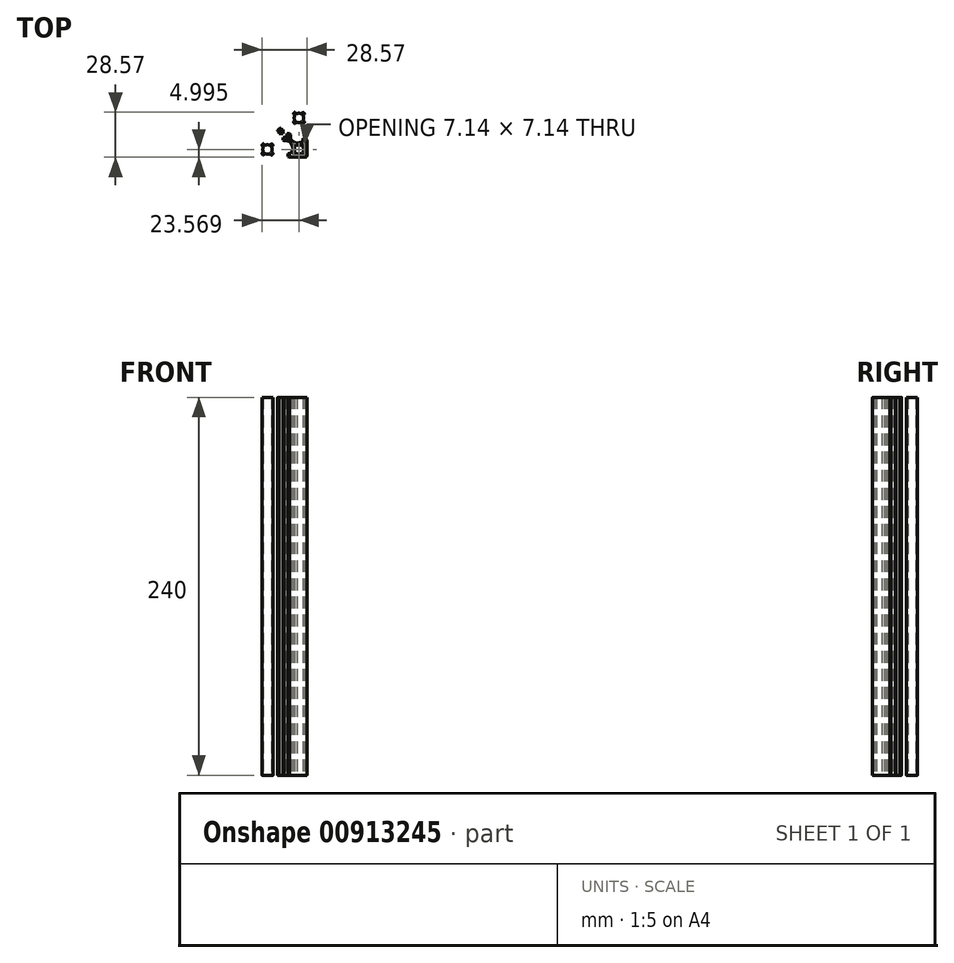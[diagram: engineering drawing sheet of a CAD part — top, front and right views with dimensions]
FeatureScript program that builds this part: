
annotation { "Feature Type Name" : "Feature", "Feature Type Description" : "" }
export const myFeature = defineFeature(function(context is Context, id is Id, definition is map)
    precondition{}
    {
        {
            var Q0;
            Q0=qCreatedBy(makeId("Top.planeOp"),FACE);
            var sketch = newSketch(context, id + "F0", { "sketchPlane" : qUnion([Q0])});
            skLineSegment(sketch, "E0", {"start": v(-2.82, -20.25) * mm, "end": v(-2.82, -15.85) * mm});
            skLineSegment(sketch, "E1", {"start": v(-5.02, -18.05) * mm, "end": v(-0.62, -18.05) * mm});
            skArc(sketch, "E2", {"start": v(-5.5, -19.39) * mm, "mid": v(-5.48, -19.57) * mm, "end": v(-5.56, -19.74) * mm});
            skLineSegment(sketch, "E3", {"start": v(-5.56, -19.74) * mm, "end": v(-6.3, -20.48) * mm});
            skArc(sketch, "E4", {"start": v(-6.3, -20.48) * mm, "mid": v(-6.4, -20.67) * mm, "end": v(-6.32, -20.88) * mm});
            skArc(sketch, "E5", {"start": v(-6.32, -20.88) * mm, "mid": v(-6, -21.24) * mm, "end": v(-5.64, -21.56) * mm});
            skArc(sketch, "E6", {"start": v(-5.64, -21.56) * mm, "mid": v(-5.44, -21.62) * mm, "end": v(-5.24, -21.54) * mm});
            skLineSegment(sketch, "E7", {"start": v(-5.24, -21.54) * mm, "end": v(-4.5, -20.8) * mm});
            skArc(sketch, "E8", {"start": v(-4.5, -20.8) * mm, "mid": v(-4.34, -20.71) * mm, "end": v(-4.16, -20.74) * mm});
            skArc(sketch, "E9", {"start": v(-4.16, -20.74) * mm, "mid": v(-2.82, -21.05) * mm, "end": v(-1.48, -20.74) * mm});
            skArc(sketch, "E10", {"start": v(-1.48, -20.74) * mm, "mid": v(-1.3, -20.71) * mm, "end": v(-1.14, -20.8) * mm});
            skLineSegment(sketch, "E11", {"start": v(-1.14, -20.8) * mm, "end": v(-0.4, -21.54) * mm});
            skArc(sketch, "E12", {"start": v(-0.4, -21.54) * mm, "mid": v(-0.2, -21.62) * mm, "end": v(0, -21.56) * mm});
            skArc(sketch, "E13", {"start": v(0, -21.56) * mm, "mid": v(0.36, -21.24) * mm, "end": v(0.68, -20.88) * mm});
            skArc(sketch, "E14", {"start": v(0.68, -20.88) * mm, "mid": v(0.75, -20.67) * mm, "end": v(0.66, -20.48) * mm});
            skLineSegment(sketch, "E15", {"start": v(0.66, -20.48) * mm, "end": v(-0.08, -19.74) * mm});
            skArc(sketch, "E16", {"start": v(-0.08, -19.74) * mm, "mid": v(-0.16, -19.57) * mm, "end": v(-0.13, -19.39) * mm});
            skArc(sketch, "E17", {"start": v(-0.13, -19.39) * mm, "mid": v(0.18, -18.05) * mm, "end": v(-0.13, -16.72) * mm});
            skArc(sketch, "E18", {"start": v(-0.13, -16.72) * mm, "mid": v(-0.16, -16.54) * mm, "end": v(-0.08, -16.37) * mm});
            skLineSegment(sketch, "E19", {"start": v(-0.08, -16.37) * mm, "end": v(0.66, -15.63) * mm});
            skArc(sketch, "E20", {"start": v(0.66, -15.63) * mm, "mid": v(0.75, -15.44) * mm, "end": v(0.68, -15.23) * mm});
            skArc(sketch, "E21", {"start": v(0.68, -15.23) * mm, "mid": v(0.36, -14.87) * mm, "end": v(0, -14.55) * mm});
            skArc(sketch, "E22", {"start": v(0, -14.55) * mm, "mid": v(-0.2, -14.48) * mm, "end": v(-0.4, -14.57) * mm});
            skLineSegment(sketch, "E23", {"start": v(-0.4, -14.57) * mm, "end": v(-1.14, -15.31) * mm});
            skArc(sketch, "E24", {"start": v(-1.14, -15.31) * mm, "mid": v(-1.3, -15.4) * mm, "end": v(-1.48, -15.37) * mm});
            skArc(sketch, "E25", {"start": v(-1.48, -15.37) * mm, "mid": v(-2.82, -15.05) * mm, "end": v(-4.16, -15.37) * mm});
            skArc(sketch, "E26", {"start": v(-4.16, -15.37) * mm, "mid": v(-4.34, -15.4) * mm, "end": v(-4.5, -15.31) * mm});
            skLineSegment(sketch, "E27", {"start": v(-4.5, -15.31) * mm, "end": v(-5.24, -14.57) * mm});
            skArc(sketch, "E28", {"start": v(-5.24, -14.57) * mm, "mid": v(-5.44, -14.48) * mm, "end": v(-5.64, -14.55) * mm});
            skArc(sketch, "E29", {"start": v(-5.64, -14.55) * mm, "mid": v(-6, -14.87) * mm, "end": v(-6.32, -15.23) * mm});
            skArc(sketch, "E30", {"start": v(-6.32, -15.23) * mm, "mid": v(-6.4, -15.44) * mm, "end": v(-6.3, -15.63) * mm});
            skLineSegment(sketch, "E31", {"start": v(-6.3, -15.63) * mm, "end": v(-5.56, -16.37) * mm});
            skArc(sketch, "E32", {"start": v(-5.56, -16.37) * mm, "mid": v(-5.48, -16.54) * mm, "end": v(-5.5, -16.72) * mm});
            skArc(sketch, "E33", {"start": v(-5.5, -16.72) * mm, "mid": v(-5.82, -18.05) * mm, "end": v(-5.5, -19.39) * mm});
            skLineSegment(sketch, "E34", {"start": v(-5.02, -38.05) * mm, "end": v(-0.62, -38.05) * mm});
            skLineSegment(sketch, "E35", {"start": v(-2.82, -35.85) * mm, "end": v(-2.82, -40.25) * mm});
            skArc(sketch, "E36", {"start": v(-5.5, -36.72) * mm, "mid": v(-5.48, -36.54) * mm, "end": v(-5.56, -36.37) * mm});
            skLineSegment(sketch, "E37", {"start": v(-5.56, -36.37) * mm, "end": v(-6.3, -35.63) * mm});
            skArc(sketch, "E38", {"start": v(-6.3, -35.63) * mm, "mid": v(-6.4, -35.44) * mm, "end": v(-6.33, -35.23) * mm});
            skArc(sketch, "E39", {"start": v(-6.33, -35.23) * mm, "mid": v(-6, -34.87) * mm, "end": v(-5.64, -34.55) * mm});
            skArc(sketch, "E40", {"start": v(-5.64, -34.55) * mm, "mid": v(-5.44, -34.48) * mm, "end": v(-5.24, -34.57) * mm});
            skLineSegment(sketch, "E41", {"start": v(-5.24, -34.57) * mm, "end": v(-4.5, -35.31) * mm});
            skArc(sketch, "E42", {"start": v(-4.5, -35.31) * mm, "mid": v(-4.34, -35.4) * mm, "end": v(-4.16, -35.37) * mm});
            skArc(sketch, "E43", {"start": v(-4.16, -35.37) * mm, "mid": v(-2.82, -35.05) * mm, "end": v(-1.48, -35.37) * mm});
            skArc(sketch, "E44", {"start": v(-1.48, -35.37) * mm, "mid": v(-1.3, -35.4) * mm, "end": v(-1.14, -35.31) * mm});
            skLineSegment(sketch, "E45", {"start": v(-1.14, -35.31) * mm, "end": v(-0.4, -34.57) * mm});
            skArc(sketch, "E46", {"start": v(-0.4, -34.57) * mm, "mid": v(-0.2, -34.48) * mm, "end": v(0, -34.55) * mm});
            skArc(sketch, "E47", {"start": v(0, -34.55) * mm, "mid": v(0.36, -34.87) * mm, "end": v(0.68, -35.23) * mm});
            skArc(sketch, "E48", {"start": v(0.68, -35.23) * mm, "mid": v(0.75, -35.44) * mm, "end": v(0.66, -35.63) * mm});
            skLineSegment(sketch, "E49", {"start": v(0.66, -35.63) * mm, "end": v(-0.08, -36.37) * mm});
            skArc(sketch, "E50", {"start": v(-0.08, -36.37) * mm, "mid": v(-0.16, -36.54) * mm, "end": v(-0.13, -36.72) * mm});
            skArc(sketch, "E51", {"start": v(-0.13, -36.72) * mm, "mid": v(0.18, -38.05) * mm, "end": v(-0.14, -39.4) * mm});
            skArc(sketch, "E52", {"start": v(-0.14, -39.4) * mm, "mid": v(-0.16, -39.57) * mm, "end": v(-0.08, -39.74) * mm});
            skLineSegment(sketch, "E53", {"start": v(-0.08, -39.74) * mm, "end": v(0.66, -40.48) * mm});
            skArc(sketch, "E54", {"start": v(0.66, -40.48) * mm, "mid": v(0.75, -40.67) * mm, "end": v(0.68, -40.88) * mm});
            skArc(sketch, "E55", {"start": v(0.68, -40.88) * mm, "mid": v(0.36, -41.24) * mm, "end": v(0, -41.56) * mm});
            skArc(sketch, "E56", {"start": v(0, -41.56) * mm, "mid": v(-0.2, -41.63) * mm, "end": v(-0.4, -41.54) * mm});
            skLineSegment(sketch, "E57", {"start": v(-0.4, -41.54) * mm, "end": v(-1.14, -40.8) * mm});
            skArc(sketch, "E58", {"start": v(-1.14, -40.8) * mm, "mid": v(-1.3, -40.71) * mm, "end": v(-1.49, -40.74) * mm});
            skArc(sketch, "E59", {"start": v(-1.49, -40.74) * mm, "mid": v(-2.82, -41.05) * mm, "end": v(-4.16, -40.74) * mm});
            skArc(sketch, "E60", {"start": v(-4.16, -40.74) * mm, "mid": v(-4.34, -40.71) * mm, "end": v(-4.5, -40.8) * mm});
            skLineSegment(sketch, "E61", {"start": v(-4.5, -40.8) * mm, "end": v(-5.24, -41.54) * mm});
            skArc(sketch, "E62", {"start": v(-5.24, -41.54) * mm, "mid": v(-5.44, -41.62) * mm, "end": v(-5.64, -41.56) * mm});
            skArc(sketch, "E63", {"start": v(-5.64, -41.56) * mm, "mid": v(-6, -41.24) * mm, "end": v(-6.33, -40.88) * mm});
            skArc(sketch, "E64", {"start": v(-6.33, -40.88) * mm, "mid": v(-6.4, -40.67) * mm, "end": v(-6.3, -40.48) * mm});
            skLineSegment(sketch, "E65", {"start": v(-6.3, -40.48) * mm, "end": v(-5.56, -39.74) * mm});
            skArc(sketch, "E66", {"start": v(-5.56, -39.74) * mm, "mid": v(-5.48, -39.57) * mm, "end": v(-5.5, -39.4) * mm});
            skArc(sketch, "E67", {"start": v(-5.5, -39.4) * mm, "mid": v(-5.82, -38.05) * mm, "end": v(-5.5, -36.72) * mm});
            skArc(sketch, "E68", {"start": v(-20.13, -36.72) * mm, "mid": v(-20.16, -36.54) * mm, "end": v(-20.07, -36.37) * mm});
            skLineSegment(sketch, "E69", {"start": v(-20.07, -36.37) * mm, "end": v(-19.33, -35.63) * mm});
            skArc(sketch, "E70", {"start": v(-19.33, -35.63) * mm, "mid": v(-19.25, -35.44) * mm, "end": v(-19.31, -35.23) * mm});
            skArc(sketch, "E71", {"start": v(-19.31, -35.23) * mm, "mid": v(-19.64, -34.87) * mm, "end": v(-20, -34.55) * mm});
            skArc(sketch, "E72", {"start": v(-20, -34.55) * mm, "mid": v(-20.2, -34.48) * mm, "end": v(-20.4, -34.57) * mm});
            skLineSegment(sketch, "E73", {"start": v(-20.4, -34.57) * mm, "end": v(-21.14, -35.31) * mm});
            skArc(sketch, "E74", {"start": v(-21.14, -35.31) * mm, "mid": v(-21.3, -35.4) * mm, "end": v(-21.48, -35.37) * mm});
            skArc(sketch, "E75", {"start": v(-21.48, -35.37) * mm, "mid": v(-22.82, -35.05) * mm, "end": v(-24.15, -35.37) * mm});
            skArc(sketch, "E76", {"start": v(-24.15, -35.37) * mm, "mid": v(-24.34, -35.4) * mm, "end": v(-24.5, -35.31) * mm});
            skLineSegment(sketch, "E77", {"start": v(-24.5, -35.31) * mm, "end": v(-25.24, -34.57) * mm});
            skArc(sketch, "E78", {"start": v(-25.24, -34.57) * mm, "mid": v(-25.44, -34.48) * mm, "end": v(-25.64, -34.55) * mm});
            skArc(sketch, "E79", {"start": v(-25.64, -34.55) * mm, "mid": v(-26, -34.87) * mm, "end": v(-26.32, -35.23) * mm});
            skArc(sketch, "E80", {"start": v(-26.32, -35.23) * mm, "mid": v(-26.39, -35.44) * mm, "end": v(-26.3, -35.63) * mm});
            skLineSegment(sketch, "E81", {"start": v(-26.3, -35.63) * mm, "end": v(-25.56, -36.37) * mm});
            skArc(sketch, "E82", {"start": v(-25.56, -36.37) * mm, "mid": v(-25.48, -36.54) * mm, "end": v(-25.5, -36.72) * mm});
            skArc(sketch, "E83", {"start": v(-25.5, -36.72) * mm, "mid": v(-25.82, -38.05) * mm, "end": v(-25.5, -39.4) * mm});
            skArc(sketch, "E84", {"start": v(-25.5, -39.4) * mm, "mid": v(-25.48, -39.57) * mm, "end": v(-25.56, -39.74) * mm});
            skLineSegment(sketch, "E85", {"start": v(-25.56, -39.74) * mm, "end": v(-26.3, -40.48) * mm});
            skArc(sketch, "E86", {"start": v(-26.3, -40.48) * mm, "mid": v(-26.39, -40.67) * mm, "end": v(-26.32, -40.88) * mm});
            skArc(sketch, "E87", {"start": v(-26.32, -40.88) * mm, "mid": v(-26, -41.24) * mm, "end": v(-25.64, -41.56) * mm});
            skArc(sketch, "E88", {"start": v(-25.64, -41.56) * mm, "mid": v(-25.44, -41.63) * mm, "end": v(-25.24, -41.54) * mm});
            skLineSegment(sketch, "E89", {"start": v(-25.24, -41.54) * mm, "end": v(-24.5, -40.8) * mm});
            skArc(sketch, "E90", {"start": v(-24.5, -40.8) * mm, "mid": v(-24.33, -40.71) * mm, "end": v(-24.15, -40.74) * mm});
            skArc(sketch, "E91", {"start": v(-24.15, -40.74) * mm, "mid": v(-22.82, -41.05) * mm, "end": v(-21.48, -40.74) * mm});
            skArc(sketch, "E92", {"start": v(-21.48, -40.74) * mm, "mid": v(-21.3, -40.71) * mm, "end": v(-21.14, -40.8) * mm});
            skLineSegment(sketch, "E93", {"start": v(-21.14, -40.8) * mm, "end": v(-20.4, -41.54) * mm});
            skArc(sketch, "E94", {"start": v(-20.4, -41.54) * mm, "mid": v(-20.2, -41.62) * mm, "end": v(-20, -41.56) * mm});
            skArc(sketch, "E95", {"start": v(-20, -41.56) * mm, "mid": v(-19.63, -41.24) * mm, "end": v(-19.31, -40.88) * mm});
            skArc(sketch, "E96", {"start": v(-19.31, -40.88) * mm, "mid": v(-19.25, -40.67) * mm, "end": v(-19.33, -40.48) * mm});
            skLineSegment(sketch, "E97", {"start": v(-19.33, -40.48) * mm, "end": v(-20.07, -39.74) * mm});
            skArc(sketch, "E98", {"start": v(-20.07, -39.74) * mm, "mid": v(-20.16, -39.57) * mm, "end": v(-20.13, -39.4) * mm});
            skArc(sketch, "E99", {"start": v(-20.13, -39.4) * mm, "mid": v(-19.82, -38.05) * mm, "end": v(-20.13, -36.72) * mm});
            skLineSegment(sketch, "E100", {"start": v(-22.82, -35.85) * mm, "end": v(-22.82, -40.25) * mm});
            skLineSegment(sketch, "E101", {"start": v(-20.62, -38.05) * mm, "end": v(-25.02, -38.05) * mm});
            skLineSegment(sketch, "E102", {"start": v(-20.62, -18.05) * mm, "end": v(-25.02, -18.05) * mm});
            skLineSegment(sketch, "E103", {"start": v(-22.82, -20.25) * mm, "end": v(-22.82, -15.85) * mm});
            skLineSegment(sketch, "E104", {"start": v(2.64, -28.05) * mm, "end": v(-29.04, -28.05) * mm});
            skLineSegment(sketch, "E105", {"start": v(-12.82, -44) * mm, "end": v(-12.82, -12.06) * mm});
            skArc(sketch, "E106", {"start": v(-9.58, -26.47) * mm, "mid": v(-9.36, -26.3) * mm, "end": v(-9.38, -26.02) * mm});
            skArc(sketch, "E107", {"start": v(-9.38, -26.02) * mm, "mid": v(-10, -25.23) * mm, "end": v(-10.78, -24.61) * mm});
            skArc(sketch, "E108", {"start": v(-10.78, -24.61) * mm, "mid": v(-11.06, -24.6) * mm, "end": v(-11.23, -24.82) * mm});
            skLineSegment(sketch, "E109", {"start": v(-11.23, -24.82) * mm, "end": v(-11.37, -25.56) * mm});
            skArc(sketch, "E110", {"start": v(-11.37, -25.56) * mm, "mid": v(-11.52, -25.77) * mm, "end": v(-11.78, -25.78) * mm});
            skArc(sketch, "E111", {"start": v(-11.78, -25.78) * mm, "mid": v(-12.82, -25.55) * mm, "end": v(-13.85, -25.78) * mm});
            skArc(sketch, "E112", {"start": v(-13.85, -25.78) * mm, "mid": v(-14.11, -25.77) * mm, "end": v(-14.27, -25.56) * mm});
            skLineSegment(sketch, "E113", {"start": v(-14.27, -25.56) * mm, "end": v(-14.4, -24.82) * mm});
            skArc(sketch, "E114", {"start": v(-14.4, -24.82) * mm, "mid": v(-14.57, -24.6) * mm, "end": v(-14.85, -24.61) * mm});
            skArc(sketch, "E115", {"start": v(-14.85, -24.61) * mm, "mid": v(-15.65, -25.23) * mm, "end": v(-16.26, -26.02) * mm});
            skArc(sketch, "E116", {"start": v(-16.26, -26.02) * mm, "mid": v(-16.27, -26.3) * mm, "end": v(-16.06, -26.47) * mm});
            skLineSegment(sketch, "E117", {"start": v(-16.06, -26.47) * mm, "end": v(-15.31, -26.6) * mm});
            skArc(sketch, "E118", {"start": v(-15.31, -26.6) * mm, "mid": v(-15.1, -26.76) * mm, "end": v(-15.1, -27.02) * mm});
            skArc(sketch, "E119", {"start": v(-15.1, -27.02) * mm, "mid": v(-15.32, -28.05) * mm, "end": v(-15.1, -29.09) * mm});
            skArc(sketch, "E120", {"start": v(-15.1, -29.09) * mm, "mid": v(-15.1, -29.35) * mm, "end": v(-15.31, -29.5) * mm});
            skLineSegment(sketch, "E121", {"start": v(-15.31, -29.5) * mm, "end": v(-16.06, -29.64) * mm});
            skArc(sketch, "E122", {"start": v(-16.06, -29.64) * mm, "mid": v(-16.27, -29.81) * mm, "end": v(-16.26, -30.09) * mm});
            skArc(sketch, "E123", {"start": v(-16.26, -30.09) * mm, "mid": v(-15.65, -30.88) * mm, "end": v(-14.85, -31.5) * mm});
            skArc(sketch, "E124", {"start": v(-14.85, -31.5) * mm, "mid": v(-14.57, -31.51) * mm, "end": v(-14.4, -31.3) * mm});
            skLineSegment(sketch, "E125", {"start": v(-14.4, -31.3) * mm, "end": v(-14.27, -30.55) * mm});
            skArc(sketch, "E126", {"start": v(-14.27, -30.55) * mm, "mid": v(-14.11, -30.34) * mm, "end": v(-13.85, -30.33) * mm});
            skArc(sketch, "E127", {"start": v(-13.85, -30.33) * mm, "mid": v(-12.82, -30.55) * mm, "end": v(-11.78, -30.33) * mm});
            skArc(sketch, "E128", {"start": v(-11.78, -30.33) * mm, "mid": v(-11.52, -30.34) * mm, "end": v(-11.37, -30.55) * mm});
            skLineSegment(sketch, "E129", {"start": v(-11.37, -30.55) * mm, "end": v(-11.23, -31.3) * mm});
            skArc(sketch, "E130", {"start": v(-11.23, -31.3) * mm, "mid": v(-11.06, -31.51) * mm, "end": v(-10.78, -31.5) * mm});
            skArc(sketch, "E131", {"start": v(-10.78, -31.5) * mm, "mid": v(-10, -30.88) * mm, "end": v(-9.38, -30.09) * mm});
            skArc(sketch, "E132", {"start": v(-9.38, -30.09) * mm, "mid": v(-9.36, -29.81) * mm, "end": v(-9.58, -29.64) * mm});
            skLineSegment(sketch, "E133", {"start": v(-9.58, -29.64) * mm, "end": v(-10.32, -29.5) * mm});
            skArc(sketch, "E134", {"start": v(-10.32, -29.5) * mm, "mid": v(-10.53, -29.35) * mm, "end": v(-10.54, -29.09) * mm});
            skArc(sketch, "E135", {"start": v(-10.54, -29.09) * mm, "mid": v(-10.32, -28.05) * mm, "end": v(-10.54, -27.02) * mm});
            skArc(sketch, "E136", {"start": v(-10.54, -27.02) * mm, "mid": v(-10.53, -26.76) * mm, "end": v(-10.32, -26.6) * mm});
            skLineSegment(sketch, "E137", {"start": v(-10.32, -26.6) * mm, "end": v(-9.58, -26.47) * mm});
            skArc(sketch, "E138", {"start": v(-20.13, -19.39) * mm, "mid": v(-20.16, -19.57) * mm, "end": v(-20.08, -19.74) * mm});
            skLineSegment(sketch, "E139", {"start": v(-20.08, -19.74) * mm, "end": v(-19.33, -20.48) * mm});
            skArc(sketch, "E140", {"start": v(-19.33, -20.48) * mm, "mid": v(-19.25, -20.67) * mm, "end": v(-19.31, -20.88) * mm});
            skArc(sketch, "E141", {"start": v(-19.31, -20.88) * mm, "mid": v(-19.64, -21.24) * mm, "end": v(-20, -21.56) * mm});
            skArc(sketch, "E142", {"start": v(-20, -21.56) * mm, "mid": v(-20.2, -21.62) * mm, "end": v(-20.4, -21.54) * mm});
            skLineSegment(sketch, "E143", {"start": v(-20.4, -21.54) * mm, "end": v(-21.14, -20.8) * mm});
            skArc(sketch, "E144", {"start": v(-21.14, -20.8) * mm, "mid": v(-21.3, -20.71) * mm, "end": v(-21.48, -20.74) * mm});
            skArc(sketch, "E145", {"start": v(-21.48, -20.74) * mm, "mid": v(-22.82, -21.05) * mm, "end": v(-24.15, -20.74) * mm});
            skArc(sketch, "E146", {"start": v(-24.15, -20.74) * mm, "mid": v(-24.34, -20.71) * mm, "end": v(-24.5, -20.8) * mm});
            skLineSegment(sketch, "E147", {"start": v(-24.5, -20.8) * mm, "end": v(-25.24, -21.54) * mm});
            skArc(sketch, "E148", {"start": v(-25.24, -21.54) * mm, "mid": v(-25.44, -21.62) * mm, "end": v(-25.64, -21.56) * mm});
            skArc(sketch, "E149", {"start": v(-25.64, -21.56) * mm, "mid": v(-26, -21.24) * mm, "end": v(-26.32, -20.88) * mm});
            skArc(sketch, "E150", {"start": v(-26.32, -20.88) * mm, "mid": v(-26.39, -20.67) * mm, "end": v(-26.3, -20.48) * mm});
            skLineSegment(sketch, "E151", {"start": v(-26.3, -20.48) * mm, "end": v(-25.56, -19.74) * mm});
            skArc(sketch, "E152", {"start": v(-25.56, -19.74) * mm, "mid": v(-25.48, -19.57) * mm, "end": v(-25.5, -19.39) * mm});
            skArc(sketch, "E153", {"start": v(-25.5, -19.39) * mm, "mid": v(-25.82, -18.05) * mm, "end": v(-25.5, -16.72) * mm});
            skArc(sketch, "E154", {"start": v(-25.5, -16.72) * mm, "mid": v(-25.48, -16.54) * mm, "end": v(-25.56, -16.37) * mm});
            skLineSegment(sketch, "E155", {"start": v(-25.56, -16.37) * mm, "end": v(-26.3, -15.63) * mm});
            skArc(sketch, "E156", {"start": v(-26.3, -15.63) * mm, "mid": v(-26.39, -15.44) * mm, "end": v(-26.32, -15.23) * mm});
            skArc(sketch, "E157", {"start": v(-26.32, -15.23) * mm, "mid": v(-26, -14.87) * mm, "end": v(-25.64, -14.55) * mm});
            skArc(sketch, "E158", {"start": v(-25.64, -14.55) * mm, "mid": v(-25.44, -14.48) * mm, "end": v(-25.24, -14.57) * mm});
            skLineSegment(sketch, "E159", {"start": v(-25.24, -14.57) * mm, "end": v(-24.5, -15.31) * mm});
            skArc(sketch, "E160", {"start": v(-24.5, -15.31) * mm, "mid": v(-24.34, -15.4) * mm, "end": v(-24.15, -15.37) * mm});
            skArc(sketch, "E161", {"start": v(-24.15, -15.37) * mm, "mid": v(-22.82, -15.05) * mm, "end": v(-21.48, -15.37) * mm});
            skArc(sketch, "E162", {"start": v(-21.48, -15.37) * mm, "mid": v(-21.3, -15.4) * mm, "end": v(-21.14, -15.31) * mm});
            skLineSegment(sketch, "E163", {"start": v(-21.14, -15.31) * mm, "end": v(-20.4, -14.57) * mm});
            skArc(sketch, "E164", {"start": v(-20.4, -14.57) * mm, "mid": v(-20.2, -14.48) * mm, "end": v(-20, -14.55) * mm});
            skArc(sketch, "E165", {"start": v(-20, -14.55) * mm, "mid": v(-19.64, -14.87) * mm, "end": v(-19.31, -15.23) * mm});
            skArc(sketch, "E166", {"start": v(-19.31, -15.23) * mm, "mid": v(-19.25, -15.44) * mm, "end": v(-19.33, -15.63) * mm});
            skLineSegment(sketch, "E167", {"start": v(-19.33, -15.63) * mm, "end": v(-20.08, -16.37) * mm});
            skArc(sketch, "E168", {"start": v(-20.08, -16.37) * mm, "mid": v(-20.16, -16.54) * mm, "end": v(-20.13, -16.72) * mm});
            skArc(sketch, "E169", {"start": v(-20.13, -16.72) * mm, "mid": v(-19.82, -18.05) * mm, "end": v(-20.13, -19.39) * mm});
            skLineSegment(sketch, "E170", {"start": v(-8.87, -43.05) * mm, "end": v(-9.67, -42.55) * mm});
            skLineSegment(sketch, "E171", {"start": v(-9.67, -42.55) * mm, "end": v(-9.67, -40.85) * mm});
            skArc(sketch, "E172", {"start": v(-9.67, -40.85) * mm, "mid": v(-9.58, -40.64) * mm, "end": v(-9.37, -40.55) * mm});
            skLineSegment(sketch, "E173", {"start": v(-9.37, -40.55) * mm, "end": v(-7.72, -40.55) * mm});
            skLineSegment(sketch, "E174", {"start": v(-7.72, -40.55) * mm, "end": v(-6.73, -37.5) * mm});
            skArc(sketch, "E175", {"start": v(-6.73, -37.5) * mm, "mid": v(-6.68, -37.24) * mm, "end": v(-6.7, -36.98) * mm});
            skArc(sketch, "E176", {"start": v(-6.7, -36.98) * mm, "mid": v(-7.54, -34.94) * mm, "end": v(-8.81, -33.14) * mm});
            skArc(sketch, "E177", {"start": v(-8.81, -33.14) * mm, "mid": v(-9.66, -32.7) * mm, "end": v(-10.6, -32.55) * mm});
            skLineSegment(sketch, "E178", {"start": v(-10.6, -32.55) * mm, "end": v(-12.32, -32.55) * mm});
            skLineSegment(sketch, "E179", {"start": v(-12.32, -32.55) * mm, "end": v(-12.82, -32.05) * mm});
            skLineSegment(sketch, "E180", {"start": v(-12.82, -32.05) * mm, "end": v(-13.32, -32.55) * mm});
            skLineSegment(sketch, "E181", {"start": v(-13.32, -32.55) * mm, "end": v(-15.04, -32.55) * mm});
            skArc(sketch, "E182", {"start": v(-15.04, -32.55) * mm, "mid": v(-15.98, -32.7) * mm, "end": v(-16.82, -33.14) * mm});
            skArc(sketch, "E183", {"start": v(-16.82, -33.14) * mm, "mid": v(-18.1, -34.94) * mm, "end": v(-18.93, -36.98) * mm});
            skArc(sketch, "E184", {"start": v(-18.93, -36.98) * mm, "mid": v(-18.95, -37.24) * mm, "end": v(-18.9, -37.5) * mm});
            skLineSegment(sketch, "E185", {"start": v(-18.9, -37.5) * mm, "end": v(-17.92, -40.55) * mm});
            skLineSegment(sketch, "E186", {"start": v(-17.92, -40.55) * mm, "end": v(-16.27, -40.55) * mm});
            skArc(sketch, "E187", {"start": v(-16.27, -40.55) * mm, "mid": v(-16.06, -40.64) * mm, "end": v(-15.97, -40.85) * mm});
            skLineSegment(sketch, "E188", {"start": v(-15.97, -40.85) * mm, "end": v(-15.97, -42.55) * mm});
            skLineSegment(sketch, "E189", {"start": v(-15.97, -42.55) * mm, "end": v(-16.77, -43.05) * mm});
            skLineSegment(sketch, "E190", {"start": v(-16.77, -43.05) * mm, "end": v(-26.82, -43.05) * mm});
            skArc(sketch, "E191", {"start": v(-26.82, -43.05) * mm, "mid": v(-27.52, -42.76) * mm, "end": v(-27.82, -42.05) * mm});
            skLineSegment(sketch, "E192", {"start": v(-27.82, -42.05) * mm, "end": v(-27.82, -32) * mm});
            skLineSegment(sketch, "E193", {"start": v(-27.82, -32) * mm, "end": v(-27.32, -31.2) * mm});
            skLineSegment(sketch, "E194", {"start": v(-27.32, -31.2) * mm, "end": v(-25.62, -31.2) * mm});
            skArc(sketch, "E195", {"start": v(-25.62, -31.2) * mm, "mid": v(-25.4, -31.3) * mm, "end": v(-25.32, -31.5) * mm});
            skLineSegment(sketch, "E196", {"start": v(-25.32, -31.5) * mm, "end": v(-25.32, -33.15) * mm});
            skLineSegment(sketch, "E197", {"start": v(-25.32, -33.15) * mm, "end": v(-22.27, -34.14) * mm});
            skArc(sketch, "E198", {"start": v(-22.27, -34.14) * mm, "mid": v(-22, -34.19) * mm, "end": v(-21.75, -34.17) * mm});
            skArc(sketch, "E199", {"start": v(-21.75, -34.17) * mm, "mid": v(-19.7, -33.33) * mm, "end": v(-17.9, -32.06) * mm});
            skArc(sketch, "E200", {"start": v(-17.9, -32.06) * mm, "mid": v(-17.47, -31.21) * mm, "end": v(-17.32, -30.27) * mm});
            skLineSegment(sketch, "E201", {"start": v(-17.32, -30.27) * mm, "end": v(-17.32, -28.55) * mm});
            skLineSegment(sketch, "E202", {"start": v(-17.32, -28.55) * mm, "end": v(-16.82, -28.05) * mm});
            skLineSegment(sketch, "E203", {"start": v(-16.82, -28.05) * mm, "end": v(-17.32, -27.55) * mm});
            skLineSegment(sketch, "E204", {"start": v(-17.32, -27.55) * mm, "end": v(-17.32, -25.84) * mm});
            skArc(sketch, "E205", {"start": v(-17.32, -25.84) * mm, "mid": v(-17.47, -24.9) * mm, "end": v(-17.9, -24.05) * mm});
            skArc(sketch, "E206", {"start": v(-17.9, -24.05) * mm, "mid": v(-19.7, -22.78) * mm, "end": v(-21.75, -21.94) * mm});
            skArc(sketch, "E207", {"start": v(-21.75, -21.94) * mm, "mid": v(-22, -21.92) * mm, "end": v(-22.27, -21.97) * mm});
            skLineSegment(sketch, "E208", {"start": v(-22.27, -21.97) * mm, "end": v(-25.32, -22.95) * mm});
            skLineSegment(sketch, "E209", {"start": v(-25.32, -22.95) * mm, "end": v(-25.32, -24.6) * mm});
            skArc(sketch, "E210", {"start": v(-25.32, -24.6) * mm, "mid": v(-25.4, -24.82) * mm, "end": v(-25.62, -24.9) * mm});
            skLineSegment(sketch, "E211", {"start": v(-25.62, -24.9) * mm, "end": v(-27.32, -24.9) * mm});
            skLineSegment(sketch, "E212", {"start": v(-27.32, -24.9) * mm, "end": v(-27.82, -24.1) * mm});
            skLineSegment(sketch, "E213", {"start": v(-27.82, -24.1) * mm, "end": v(-27.82, -14.05) * mm});
            skArc(sketch, "E214", {"start": v(-27.82, -14.05) * mm, "mid": v(-27.52, -13.35) * mm, "end": v(-26.82, -13.05) * mm});
            skLineSegment(sketch, "E215", {"start": v(-26.82, -13.05) * mm, "end": v(-16.77, -13.05) * mm});
            skLineSegment(sketch, "E216", {"start": v(-16.77, -13.05) * mm, "end": v(-15.97, -13.55) * mm});
            skLineSegment(sketch, "E217", {"start": v(-15.97, -13.55) * mm, "end": v(-15.97, -15.25) * mm});
            skArc(sketch, "E218", {"start": v(-15.97, -15.25) * mm, "mid": v(-16.06, -15.47) * mm, "end": v(-16.27, -15.55) * mm});
            skLineSegment(sketch, "E219", {"start": v(-16.27, -15.55) * mm, "end": v(-17.92, -15.55) * mm});
            skLineSegment(sketch, "E220", {"start": v(-17.92, -15.55) * mm, "end": v(-18.9, -18.6) * mm});
            skArc(sketch, "E221", {"start": v(-18.9, -18.6) * mm, "mid": v(-18.95, -18.86) * mm, "end": v(-18.93, -19.13) * mm});
            skArc(sketch, "E222", {"start": v(-18.93, -19.13) * mm, "mid": v(-18.1, -21.16) * mm, "end": v(-16.82, -22.96) * mm});
            skArc(sketch, "E223", {"start": v(-16.82, -22.96) * mm, "mid": v(-15.98, -23.4) * mm, "end": v(-15.04, -23.55) * mm});
            skLineSegment(sketch, "E224", {"start": v(-15.04, -23.55) * mm, "end": v(-13.32, -23.55) * mm});
            skLineSegment(sketch, "E225", {"start": v(-13.32, -23.55) * mm, "end": v(-12.82, -24.05) * mm});
            skLineSegment(sketch, "E226", {"start": v(-12.82, -24.05) * mm, "end": v(-12.32, -23.55) * mm});
            skLineSegment(sketch, "E227", {"start": v(-12.32, -23.55) * mm, "end": v(-10.6, -23.55) * mm});
            skArc(sketch, "E228", {"start": v(-10.6, -23.55) * mm, "mid": v(-9.66, -23.4) * mm, "end": v(-8.81, -22.96) * mm});
            skArc(sketch, "E229", {"start": v(-8.81, -22.96) * mm, "mid": v(-7.54, -21.16) * mm, "end": v(-6.7, -19.13) * mm});
            skArc(sketch, "E230", {"start": v(-6.7, -19.13) * mm, "mid": v(-6.68, -18.86) * mm, "end": v(-6.73, -18.6) * mm});
            skLineSegment(sketch, "E231", {"start": v(-6.73, -18.6) * mm, "end": v(-7.72, -15.55) * mm});
            skLineSegment(sketch, "E232", {"start": v(-7.72, -15.55) * mm, "end": v(-9.37, -15.55) * mm});
            skArc(sketch, "E233", {"start": v(-9.37, -15.55) * mm, "mid": v(-9.58, -15.47) * mm, "end": v(-9.67, -15.25) * mm});
            skLineSegment(sketch, "E234", {"start": v(-9.67, -15.25) * mm, "end": v(-9.67, -13.55) * mm});
            skLineSegment(sketch, "E235", {"start": v(-9.67, -13.55) * mm, "end": v(-8.87, -13.05) * mm});
            skLineSegment(sketch, "E236", {"start": v(-8.87, -13.05) * mm, "end": v(1.18, -13.05) * mm});
            skArc(sketch, "E237", {"start": v(1.18, -13.05) * mm, "mid": v(1.89, -13.35) * mm, "end": v(2.18, -14.05) * mm});
            skLineSegment(sketch, "E238", {"start": v(2.18, -14.05) * mm, "end": v(2.18, -24.1) * mm});
            skLineSegment(sketch, "E239", {"start": v(2.18, -24.1) * mm, "end": v(1.68, -24.9) * mm});
            skLineSegment(sketch, "E240", {"start": v(1.68, -24.9) * mm, "end": v(-0.02, -24.9) * mm});
            skArc(sketch, "E241", {"start": v(-0.02, -24.9) * mm, "mid": v(-0.23, -24.82) * mm, "end": v(-0.32, -24.6) * mm});
            skLineSegment(sketch, "E242", {"start": v(-0.32, -24.6) * mm, "end": v(-0.32, -22.95) * mm});
            skLineSegment(sketch, "E243", {"start": v(-0.32, -22.95) * mm, "end": v(-3.37, -21.97) * mm});
            skArc(sketch, "E244", {"start": v(-3.37, -21.97) * mm, "mid": v(-3.63, -21.92) * mm, "end": v(-3.9, -21.94) * mm});
            skArc(sketch, "E245", {"start": v(-3.9, -21.94) * mm, "mid": v(-5.93, -22.78) * mm, "end": v(-7.73, -24.05) * mm});
            skArc(sketch, "E246", {"start": v(-7.73, -24.05) * mm, "mid": v(-8.17, -24.9) * mm, "end": v(-8.32, -25.84) * mm});
            skLineSegment(sketch, "E247", {"start": v(-8.32, -25.84) * mm, "end": v(-8.32, -27.55) * mm});
            skLineSegment(sketch, "E248", {"start": v(-8.32, -27.55) * mm, "end": v(-8.82, -28.05) * mm});
            skLineSegment(sketch, "E249", {"start": v(-8.82, -28.05) * mm, "end": v(-8.32, -28.55) * mm});
            skLineSegment(sketch, "E250", {"start": v(-8.32, -28.55) * mm, "end": v(-8.32, -30.27) * mm});
            skArc(sketch, "E251", {"start": v(-8.32, -30.27) * mm, "mid": v(-8.17, -31.21) * mm, "end": v(-7.73, -32.06) * mm});
            skArc(sketch, "E252", {"start": v(-7.73, -32.06) * mm, "mid": v(-5.93, -33.33) * mm, "end": v(-3.9, -34.17) * mm});
            skArc(sketch, "E253", {"start": v(-3.9, -34.17) * mm, "mid": v(-3.63, -34.19) * mm, "end": v(-3.37, -34.14) * mm});
            skLineSegment(sketch, "E254", {"start": v(-3.37, -34.14) * mm, "end": v(-0.32, -33.15) * mm});
            skLineSegment(sketch, "E255", {"start": v(-0.32, -33.15) * mm, "end": v(-0.32, -31.5) * mm});
            skArc(sketch, "E256", {"start": v(-0.32, -31.5) * mm, "mid": v(-0.23, -31.3) * mm, "end": v(-0.02, -31.2) * mm});
            skLineSegment(sketch, "E257", {"start": v(-0.02, -31.2) * mm, "end": v(1.68, -31.2) * mm});
            skLineSegment(sketch, "E258", {"start": v(1.68, -31.2) * mm, "end": v(2.18, -32) * mm});
            skLineSegment(sketch, "E259", {"start": v(2.18, -32) * mm, "end": v(2.18, -42.05) * mm});
            skArc(sketch, "E260", {"start": v(2.18, -42.05) * mm, "mid": v(1.89, -42.76) * mm, "end": v(1.18, -43.05) * mm});
            skLineSegment(sketch, "E261", {"start": v(1.18, -43.05) * mm, "end": v(-8.87, -43.05) * mm});
            skSolve(sketch);
        }
        {
            var Q0;
            {var subQ1=sQuery(id+"F0.wireOp",EDGE,"E112");Q0=makeQuery(id+"F0.imprint","IMPRINT",FACE,{"disambiguationData":[TD([[makeQuery(id+"F0.imprint","IMPRINT",EDGE,{"derivedFrom":subQ1}),-1.0]])]});}
            var Q1;
            Q1=makeQuery(id+"F0.imprint","IMPRINT",FACE,{"disambiguationData":[TD([[makeQuery(id+"F0.imprint","IMPRINT",EDGE,{"derivedFrom":sQuery(id+"F0.wireOp",EDGE,"E2")}),-1.0]])]});
            var Q2;
            Q2=makeQuery(id+"F0.imprint","IMPRINT",FACE,{"disambiguationData":[TD([[makeQuery(id+"F0.imprint","IMPRINT",EDGE,{"derivedFrom":sQuery(id+"F0.wireOp",EDGE,"E36")}),1.0]])]});
            var Q3;
            Q3=makeQuery(id+"F0.imprint","IMPRINT",FACE,{"disambiguationData":[TD([[makeQuery(id+"F0.imprint","IMPRINT",EDGE,{"derivedFrom":sQuery(id+"F0.wireOp",EDGE,"E68")}),-1.0]])]});
            extrude(context, id + "F1", {"entities" : qUnion([Q0, Q1, Q2, Q3]), "depth" : 240 * mm, "offsetDistance" : 25 * mm});
        }
    });
